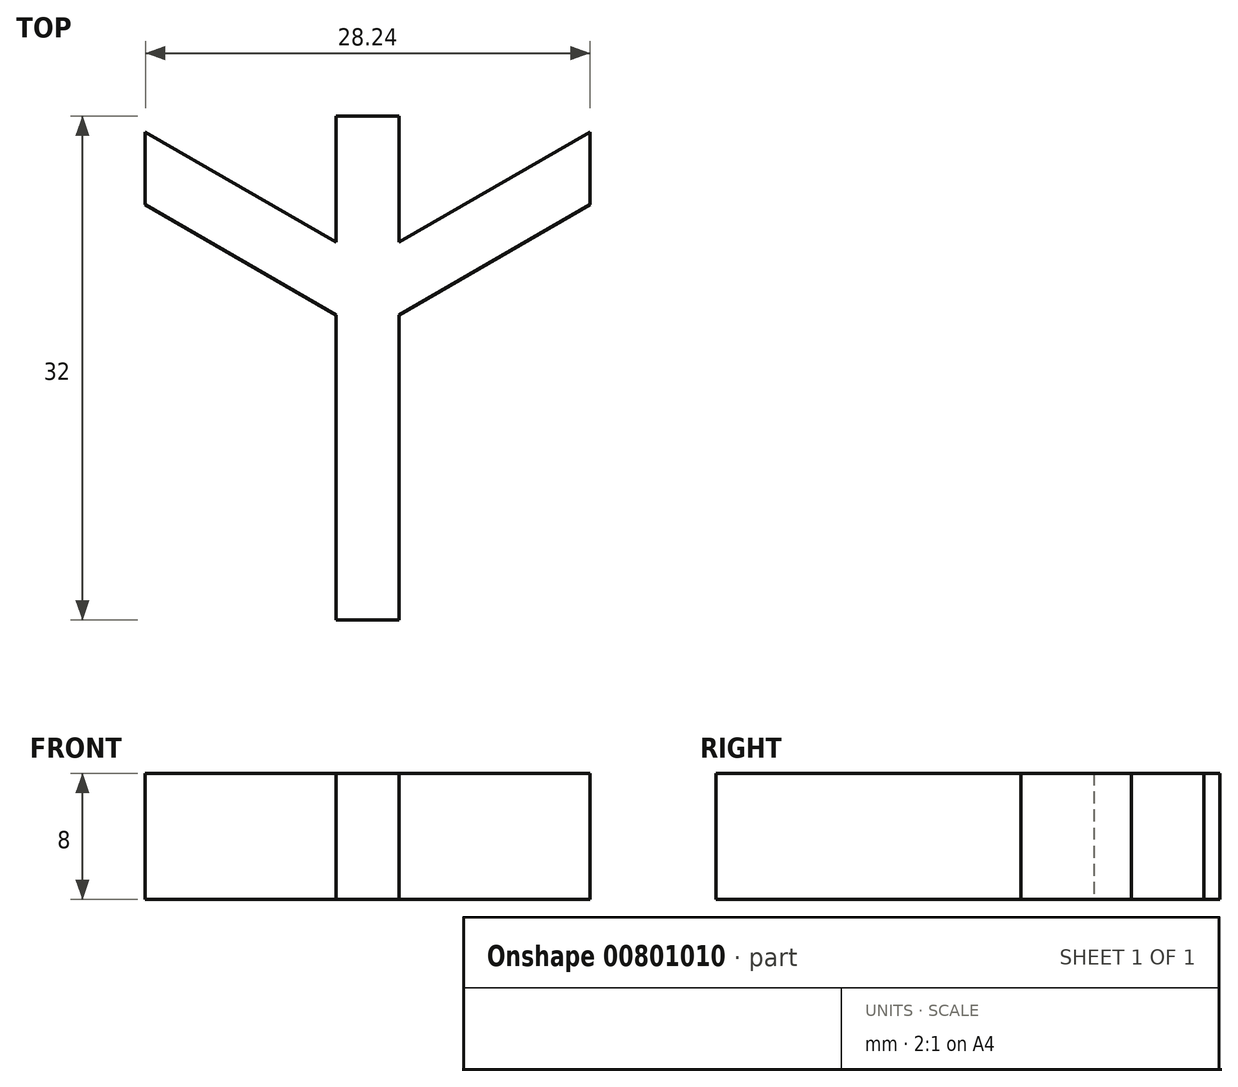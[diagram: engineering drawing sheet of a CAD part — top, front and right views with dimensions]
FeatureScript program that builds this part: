
annotation { "Feature Type Name" : "Feature", "Feature Type Description" : "" }
export const myFeature = defineFeature(function(context is Context, id is Id, definition is map)
    precondition{}
    {
        {
            var Q0;
            Q0=qCreatedBy(makeId("Top.planeOp"),FACE);
            var sketch = newSketch(context, id + "F0", { "sketchPlane" : qUnion([Q0])});
            skLineSegment(sketch, "E0", {"start": v(0, 0) * mm, "end": v(0, -8) * mm});
            skLineSegment(sketch, "E1", {"start": v(0, -8) * mm, "end": v(-12.12, -1) * mm});
            skLineSegment(sketch, "E2", {"start": v(-12.12, -1) * mm, "end": v(-12.12, -5.62) * mm});
            skLineSegment(sketch, "E3", {"start": v(-12.12, -5.62) * mm, "end": v(0, -12.62) * mm});
            skLineSegment(sketch, "E4", {"start": v(0, -12.62) * mm, "end": v(0, -32) * mm});
            skLineSegment(sketch, "E5", {"start": v(0, -32) * mm, "end": v(4, -32) * mm});
            skLineSegment(sketch, "E6", {"start": v(4, -32) * mm, "end": v(4, -12.62) * mm});
            skLineSegment(sketch, "E7", {"start": v(4, -8) * mm, "end": v(4, 0) * mm});
            skLineSegment(sketch, "E8", {"start": v(4, 0) * mm, "end": v(0, 0) * mm});
            skLineSegment(sketch, "E9", {"start": v(4, -8) * mm, "end": v(16.12, -1) * mm});
            skLineSegment(sketch, "E10", {"start": v(16.12, -1) * mm, "end": v(16.12, -5.62) * mm});
            skLineSegment(sketch, "E11", {"start": v(16.12, -5.62) * mm, "end": v(4, -12.62) * mm});
            skSolve(sketch);
        }
        {
            var Q0;
            Q0=makeQuery(id+"F0.imprint","IMPRINT",FACE,{"disambiguationData":[TD([[makeQuery(id+"F0.imprint","IMPRINT",EDGE,{"derivedFrom":sQuery(id+"F0.wireOp",EDGE,"E0")}),1.0]])]});
            extrude(context, id + "F1", {"entities" : qUnion([Q0]), "depth" : 8 * mm, "offsetDistance" : 25 * mm});
        }
    });
